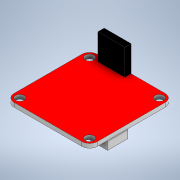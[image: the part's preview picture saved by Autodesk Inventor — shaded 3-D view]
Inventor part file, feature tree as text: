
AUTODESK INVENTOR PART (.ipt)
format: ipt  version: 2020 (Build 240168000, 168)  size: 176,640 bytes
history: native  units: mm
features: extrude x3, sketch x3, projected_geometry x2, other x1
ambient origin geometry x8: Origin, YZ Plane, XZ Plane, XY Plane, X Axis, Y Axis, Z Axis, Center Point
bodies: Body1 (feature_tree)
feature tree (9):
  other  "Твердое тело1"
  extrude  "Выдавливание1"  Depth=32.0mm
  extrude  "Выдавливание2"  Depth=32.0mm
  extrude  "Выдавливание3"  Depth=3.25mm
  sketch  "Эскиз1"
  sketch  "Эскиз2"
  projected_geometry  "Спроецированная петля1"
  sketch  "Эскиз3"
  projected_geometry  "Спроецированная петля2"
